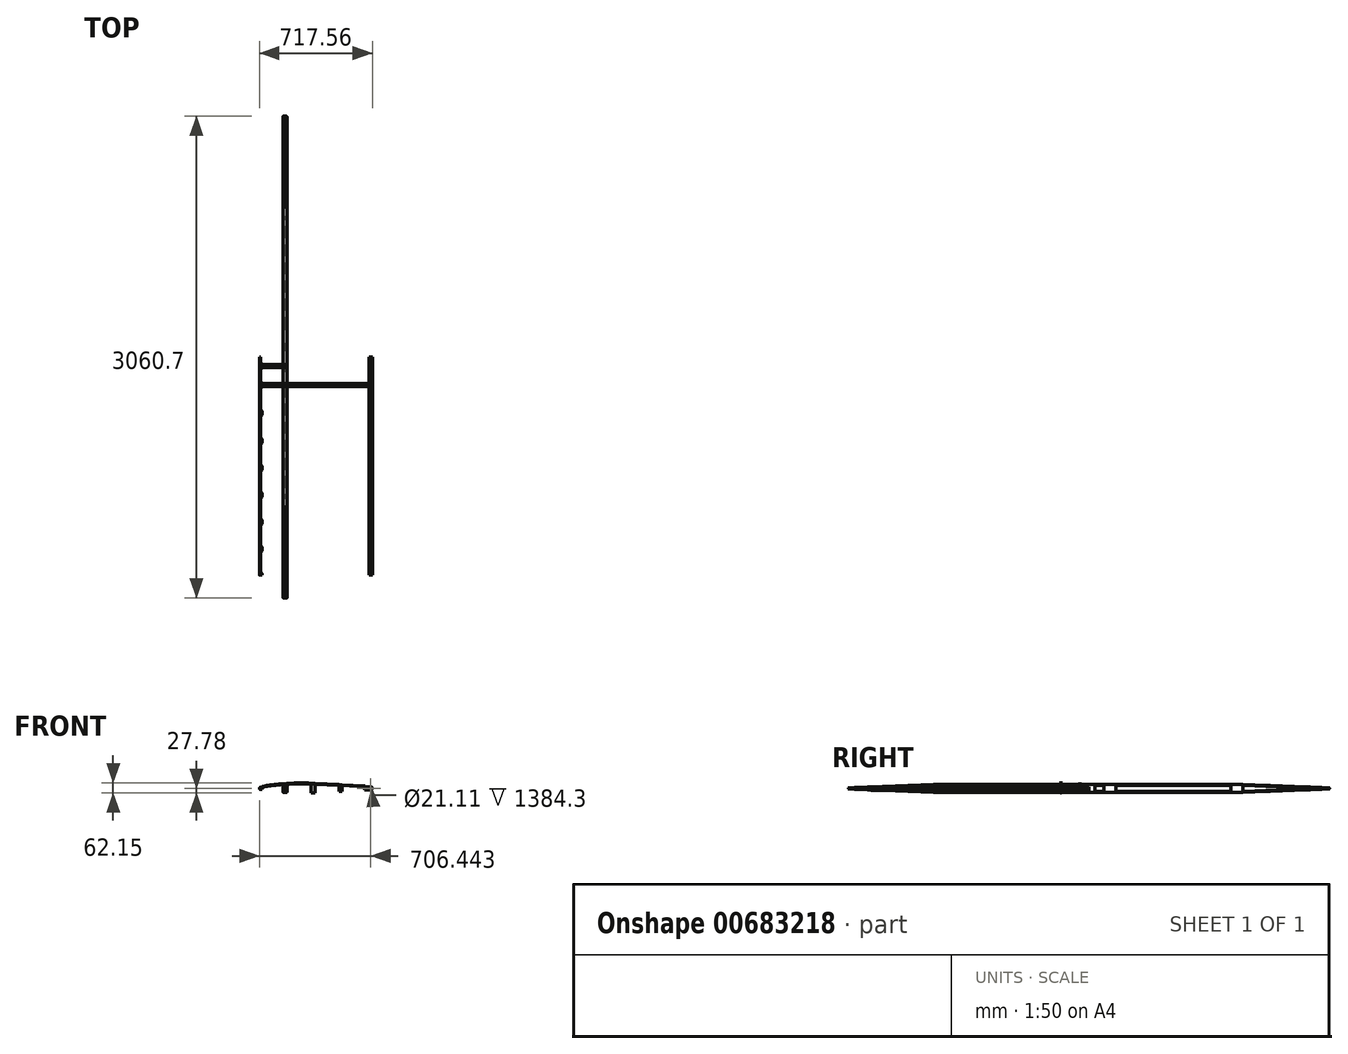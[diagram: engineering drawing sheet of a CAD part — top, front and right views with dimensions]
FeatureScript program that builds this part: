
annotation { "Feature Type Name" : "Feature", "Feature Type Description" : "" }
export const myFeature = defineFeature(function(context is Context, id is Id, definition is map)
    precondition{}
    {
        {
            var Q0;
            Q0=qCreatedBy(makeId("Front.planeOp"),FACE);
            var sketch = newSketch(context, id + "F0", { "sketchPlane" : qUnion([Q0])});
            skLineSegment(sketch, "E0", {"start": v(-12.7, 23.81) * mm, "end": v(12.7, 25.4) * mm});
            skLineSegment(sketch, "E1", {"start": v(12.7, 25.4) * mm, "end": v(12.7, -25.4) * mm});
            skLineSegment(sketch, "E2", {"start": v(12.7, -25.4) * mm, "end": v(-12.7, -23.81) * mm});
            skLineSegment(sketch, "E3", {"start": v(-12.7, -23.81) * mm, "end": v(-12.7, 23.81) * mm});
            skCircle(sketch, "E4", {"center": v(544.51, 0) * mm, "radius": 10.55 * mm});
            skCircle(sketch, "E5", {"center": v(544.51, 0) * mm, "radius": 11.11 * mm});
            skArc(sketch, "E6", {"start": v(-154.56, 7.92) * mm, "mid": v(-161.92, 0) * mm, "end": v(-154.56, -7.92) * mm});
            skLineSegment(sketch, "E7", {"start": v(-154.56, 7.92) * mm, "end": v(-153.99, 5.16) * mm});
            skLineSegment(sketch, "E8", {"start": v(-153.99, -5.16) * mm, "end": v(-154.56, -7.92) * mm});
            skLineSegment(sketch, "E9", {"start": v(-153.99, 5.16) * mm, "end": v(-144.46, 7.14) * mm});
            skLineSegment(sketch, "E10", {"start": v(-144.46, 7.14) * mm, "end": v(-144.46, -7.14) * mm});
            skLineSegment(sketch, "E11", {"start": v(-144.46, -7.14) * mm, "end": v(-153.99, -5.16) * mm});
            skLineSegment(sketch, "E12", {"start": v(-161.93, 0) * mm, "end": v(-161.93, -20.21) * mm, "construction": true});
            skPoint(sketch, "E12.startSnap0", {"position": v(-161.93, 0) * mm});
            skLineSegment(sketch, "E13", {"start": v(-153.99, 5.16) * mm, "end": v(-153.99, -5.16) * mm, "construction": true});
            skLineSegment(sketch, "E14", {"start": v(-161.93, 0) * mm, "end": v(-144.46, 0) * mm, "construction": true});
            skSolve(sketch);
        }
        {
            var Q0;
            Q0=makeQuery(id+"F0.imprint","IMPRINT",FACE,{"disambiguationData":[TD([[makeQuery(id+"F0.imprint","IMPRINT",EDGE,{"derivedFrom":sQuery(id+"F0.wireOp",EDGE,"E0")}),-1.0]])]});
            extrude(context, id + "F1", {"entities" : qUnion([Q0]), "depth" : 952.5 * mm, "offsetDistance" : 25.4 * mm});
        }
        {
            var Q0;
            Q0=makeQuery(id+"F1.opExtrude","SWEPT_FACE",FACE,{"disambiguationData":[OSD([sQuery(id+"F0.wireOp",EDGE,"E3")])]});
            var sketch = newSketch(context, id + "F2", { "sketchPlane" : qUnion([Q0])});
            skLineSegment(sketch, "E15", {"start": v(952.5, 23.81) * mm, "end": v(1530.35, 3.17) * mm});
            skLineSegment(sketch, "E16", {"start": v(952.5, -23.81) * mm, "end": v(1530.35, -3.17) * mm});
            skArc(sketch, "E17", {"start": v(1530.35, 3.18) * mm, "mid": v(1527.18, 0) * mm, "end": v(1530.35, -3.18) * mm});
            skLineSegment(sketch, "E18", {"start": v(1530.35, 0) * mm, "end": v(1530.35, 10.29) * mm, "construction": true});
            skArc(sketch, "E19", {"start": v(1531, 3.1) * mm, "mid": v(1527.18, 0) * mm, "end": v(1531, -3.1) * mm});
            skArc(sketch, "E20", {"start": v(1538.67, 1.5) * mm, "mid": v(1539.88, 0) * mm, "end": v(1538.67, -1.5) * mm});
            skLineSegment(sketch, "E21", {"start": v(1531, 3.1) * mm, "end": v(1538.67, 1.5) * mm});
            skLineSegment(sketch, "E22", {"start": v(1531, -3.1) * mm, "end": v(1538.67, -1.5) * mm});
            skLineSegment(sketch, "E23", {"start": v(1527.18, 0) * mm, "end": v(1527.18, 5.45) * mm, "construction": true});
            skLineSegment(sketch, "E24", {"start": v(1539.88, 0) * mm, "end": v(1539.88, 5.45) * mm, "construction": true});
            skSolve(sketch);
        }
        {
            var Q0;
            Q0=makeQuery(id+"F1.opExtrude","SWEPT_FACE",FACE,{"disambiguationData":[OSD([sQuery(id+"F0.wireOp",EDGE,"E1")])]});
            var sketch = newSketch(context, id + "F3", { "sketchPlane" : qUnion([Q0])});
            skLineSegment(sketch, "E25", {"start": v(-952.5, 25.4) * mm, "end": v(-1530.35, 3.17) * mm});
            skLineSegment(sketch, "E26", {"start": v(-952.5, -25.4) * mm, "end": v(-1530.35, -3.17) * mm});
            skArc(sketch, "E27", {"start": v(-1530.35, 3.18) * mm, "mid": v(-1527.18, 0) * mm, "end": v(-1530.35, -3.18) * mm});
            skSolve(sketch);
        }
        {
            var Q1;
            {var subQ0=sQuery(id+"F2.wireOp",EDGE,"E15");Q1=makeQuery(id+"F2.imprint","IMPRINT",FACE,{"disambiguationData":[TD([[makeQuery(id+"F2.imprint","IMPRINT",EDGE,{"derivedFrom":subQ0}),-1.0]])]});}
            var Q2;
            Q2=makeQuery(id+"F3.imprint","IMPRINT",FACE,{"disambiguationData":[TD([[makeQuery(id+"F3.imprint","IMPRINT",EDGE,{"derivedFrom":sQuery(id+"F3.wireOp",EDGE,"E25")}),1.0]])]});
            loft(context, id + "F4", {"operationType" : NewBodyOperationType.ADD, "sheetProfilesArray" : [{ "sheetProfileEntities" : qUnion([Q1]) }, { "sheetProfileEntities" : qUnion([Q2]) }]});
        }
        {
            var Q0;
            {var subQ0=sQuery(id+"F2.wireOp",EDGE,"E15");var subQ2=sQuery(id+"F0.wireOp",EDGE,"E3");Q0=makeQuery(id+"F4.boolean.opBoolean","MERGE",FACE,{"derivedFrom":[makeQuery(id+"F1.opExtrude","SWEPT_FACE",FACE,{"disambiguationData":[OSD([subQ2])]}),makeQuery(id+"F4.opLoft","CAP_FACE",FACE,{"disambiguationData":[OSD([makeQuery(id+"F2.imprint","IMPRINT",FACE,{"disambiguationData":[TD([[makeQuery(id+"F2.imprint","IMPRINT",EDGE,{"derivedFrom":subQ0}),-1.0]])]})])],"isStart":true})]});}
            var sketch = newSketch(context, id + "F5", { "sketchPlane" : qUnion([Q0])});
            skLineSegment(sketch, "E28.bottom", {"start": v(44.45, 17.46) * mm, "end": v(88.9, 17.46) * mm});
            skLineSegment(sketch, "E28.top", {"start": v(44.45, -17.46) * mm, "end": v(88.9, -17.46) * mm});
            skLineSegment(sketch, "E28.left", {"start": v(38.1, 11.11) * mm, "end": v(38.1, -11.11) * mm});
            skLineSegment(sketch, "E28.right", {"start": v(95.25, 11.11) * mm, "end": v(95.25, -11.11) * mm});
            skPoint(sketch, "E29.visualSharp", {"position": v(38.1, 17.46) * mm});
            skArc(sketch, "E29.filletArc", {"start": v(44.45, 17.46) * mm, "mid": v(39.96, 15.6) * mm, "end": v(38.1, 11.11) * mm});
            skPoint(sketch, "E30.visualSharp", {"position": v(95.25, -17.46) * mm});
            skArc(sketch, "E30.filletArc", {"start": v(88.9, -17.46) * mm, "mid": v(93.4, -15.6) * mm, "end": v(95.25, -11.11) * mm});
            skPoint(sketch, "E31.visualSharp", {"position": v(95.25, 17.46) * mm});
            skArc(sketch, "E31.filletArc", {"start": v(95.25, 11.11) * mm, "mid": v(93.4, 15.6) * mm, "end": v(88.9, 17.46) * mm});
            skPoint(sketch, "E32.visualSharp", {"position": v(38.1, -17.46) * mm});
            skArc(sketch, "E32.filletArc", {"start": v(38.1, -11.11) * mm, "mid": v(39.96, -15.6) * mm, "end": v(44.45, -17.46) * mm});
            skLineSegment(sketch, "E33.bottom", {"start": v(177.8, 17.46) * mm, "end": v(895.35, 17.46) * mm});
            skLineSegment(sketch, "E33.top", {"start": v(177.8, -17.46) * mm, "end": v(895.35, -17.46) * mm});
            skLineSegment(sketch, "E33.left", {"start": v(171.45, 11.11) * mm, "end": v(171.45, -11.11) * mm});
            skLineSegment(sketch, "E33.right", {"start": v(901.7, 11.11) * mm, "end": v(901.7, -11.11) * mm});
            skPoint(sketch, "E34.visualSharp", {"position": v(171.45, 17.46) * mm});
            skArc(sketch, "E34.filletArc", {"start": v(177.8, 17.46) * mm, "mid": v(173.3, 15.6) * mm, "end": v(171.45, 11.11) * mm});
            skPoint(sketch, "E35.visualSharp", {"position": v(171.45, -17.46) * mm});
            skArc(sketch, "E35.filletArc", {"start": v(171.45, -11.11) * mm, "mid": v(173.3, -15.6) * mm, "end": v(177.8, -17.46) * mm});
            skPoint(sketch, "E36.visualSharp", {"position": v(901.7, 17.46) * mm});
            skArc(sketch, "E36.filletArc", {"start": v(901.7, 11.11) * mm, "mid": v(899.84, 15.6) * mm, "end": v(895.35, 17.46) * mm});
            skPoint(sketch, "E37.visualSharp", {"position": v(901.7, -17.46) * mm});
            skArc(sketch, "E37.filletArc", {"start": v(895.35, -17.46) * mm, "mid": v(899.84, -15.6) * mm, "end": v(901.7, -11.11) * mm});
            skLineSegment(sketch, "E38", {"start": v(977.9, 9.97) * mm, "end": v(977.9, -9.97) * mm});
            skLineSegment(sketch, "E39", {"start": v(984.48, -16.32) * mm, "end": v(1329.65, -3.99) * mm});
            skLineSegment(sketch, "E40", {"start": v(1329.65, 3.99) * mm, "end": v(984.48, 16.32) * mm});
            skPoint(sketch, "E41.visualSharp", {"position": v(1441.34, 0) * mm});
            skArc(sketch, "E41.filletArc", {"start": v(1329.65, -3.99) * mm, "mid": v(1333.5, 0) * mm, "end": v(1329.65, 3.99) * mm});
            skPoint(sketch, "E42.visualSharp", {"position": v(977.9, 16.55) * mm});
            skArc(sketch, "E42.filletArc", {"start": v(984.48, 16.32) * mm, "mid": v(979.84, 14.54) * mm, "end": v(977.9, 9.97) * mm});
            skPoint(sketch, "E43.visualSharp", {"position": v(977.9, -16.55) * mm});
            skArc(sketch, "E43.filletArc", {"start": v(977.9, -9.97) * mm, "mid": v(979.84, -14.54) * mm, "end": v(984.48, -16.32) * mm});
            skLineSegment(sketch, "E44", {"start": v(1333.5, 0) * mm, "end": v(1333.5, 29.1) * mm, "construction": true});
            skSolve(sketch);
        }
        {
            var Q0;
            Q0 = qSketchRegion(id + "F5", true);
            extrude(context, id + "F6", {"entities" : qUnion([Q0]), "operationType" : NewBodyOperationType.REMOVE, "oppositeDirection" : true, "depth" : 5 / 406.4 * mm, "offsetDistance" : 25.4 * mm});
        }
        {
            var Q0;
            {var subQ0=sQuery(id+"F0.wireOp",EDGE,"E1");Q0=makeQuery(id+"F4.boolean.opBoolean","MERGE",FACE,{"derivedFrom":[makeQuery(id+"F1.opExtrude","SWEPT_FACE",FACE,{"disambiguationData":[OSD([subQ0])]}),makeQuery(id+"F4.opLoft","CAP_FACE",FACE,{"disambiguationData":[OSD([makeQuery(id+"F3.imprint","IMPRINT",FACE,{"disambiguationData":[TD([[makeQuery(id+"F3.imprint","IMPRINT",EDGE,{"derivedFrom":sQuery(id+"F3.wireOp",EDGE,"E25")}),1.0]])]})])],"isStart":true})]});}
            var sketch = newSketch(context, id + "F7", { "sketchPlane" : qUnion([Q0])});
            skLineSegment(sketch, "E45.bottom", {"start": v(-88.9, 19.05) * mm, "end": v(-44.45, 19.05) * mm});
            skLineSegment(sketch, "E45.top", {"start": v(-88.9, -19.05) * mm, "end": v(-44.45, -19.05) * mm});
            skLineSegment(sketch, "E45.left", {"start": v(-95.25, 12.7) * mm, "end": v(-95.25, -12.7) * mm});
            skLineSegment(sketch, "E45.right", {"start": v(-38.1, 12.7) * mm, "end": v(-38.1, -12.7) * mm});
            skPoint(sketch, "E46.visualSharp", {"position": v(-95.25, 19.05) * mm});
            skArc(sketch, "E46.filletArc", {"start": v(-88.9, 19.05) * mm, "mid": v(-93.4, 17.2) * mm, "end": v(-95.25, 12.7) * mm});
            skPoint(sketch, "E47.visualSharp", {"position": v(-95.25, -19.05) * mm});
            skArc(sketch, "E47.filletArc", {"start": v(-95.25, -12.7) * mm, "mid": v(-93.4, -17.2) * mm, "end": v(-88.9, -19.05) * mm});
            skPoint(sketch, "E48.visualSharp", {"position": v(-38.1, -19.05) * mm});
            skArc(sketch, "E48.filletArc", {"start": v(-44.45, -19.05) * mm, "mid": v(-39.96, -17.2) * mm, "end": v(-38.1, -12.7) * mm});
            skPoint(sketch, "E49.visualSharp", {"position": v(-38.1, 19.05) * mm});
            skArc(sketch, "E49.filletArc", {"start": v(-38.1, 12.7) * mm, "mid": v(-39.96, 17.2) * mm, "end": v(-44.45, 19.05) * mm});
            skLineSegment(sketch, "E50.bottom", {"start": v(-177.8, 19.05) * mm, "end": v(-895.35, 19.05) * mm});
            skLineSegment(sketch, "E50.top", {"start": v(-177.8, -19.05) * mm, "end": v(-895.35, -19.05) * mm});
            skLineSegment(sketch, "E50.left", {"start": v(-171.45, 12.7) * mm, "end": v(-171.45, -12.7) * mm});
            skLineSegment(sketch, "E50.right", {"start": v(-901.7, 12.7) * mm, "end": v(-901.7, -12.7) * mm});
            skPoint(sketch, "E51.visualSharp", {"position": v(-901.7, 19.05) * mm});
            skArc(sketch, "E51.filletArc", {"start": v(-895.35, 19.05) * mm, "mid": v(-899.84, 17.2) * mm, "end": v(-901.7, 12.7) * mm});
            skPoint(sketch, "E52.visualSharp", {"position": v(-901.7, -19.05) * mm});
            skArc(sketch, "E52.filletArc", {"start": v(-901.7, -12.7) * mm, "mid": v(-899.84, -17.2) * mm, "end": v(-895.35, -19.05) * mm});
            skPoint(sketch, "E53.visualSharp", {"position": v(-171.45, 19.05) * mm});
            skArc(sketch, "E53.filletArc", {"start": v(-171.45, 12.7) * mm, "mid": v(-173.3, 17.2) * mm, "end": v(-177.8, 19.05) * mm});
            skPoint(sketch, "E54.visualSharp", {"position": v(-171.45, -19.05) * mm});
            skArc(sketch, "E54.filletArc", {"start": v(-177.8, -19.05) * mm, "mid": v(-173.3, -17.2) * mm, "end": v(-171.45, -12.7) * mm});
            skLineSegment(sketch, "E55", {"start": v(-977.9, 11.47) * mm, "end": v(-977.9, -11.47) * mm});
            skLineSegment(sketch, "E56", {"start": v(-984.5, -17.81) * mm, "end": v(-1329.68, -4.54) * mm});
            skLineSegment(sketch, "E57", {"start": v(-984.5, 17.81) * mm, "end": v(-1329.68, 4.54) * mm});
            skPoint(sketch, "E58.visualSharp", {"position": v(-977.9, 18.07) * mm});
            skArc(sketch, "E58.filletArc", {"start": v(-977.9, 11.47) * mm, "mid": v(-979.85, 16.05) * mm, "end": v(-984.5, 17.81) * mm});
            skPoint(sketch, "E59.visualSharp", {"position": v(-977.9, -18.07) * mm});
            skArc(sketch, "E59.filletArc", {"start": v(-984.5, -17.81) * mm, "mid": v(-979.85, -16.05) * mm, "end": v(-977.9, -11.47) * mm});
            skArc(sketch, "E60.filletArc", {"start": v(-1329.68, 4.54) * mm, "mid": v(-1334.05, 0) * mm, "end": v(-1329.68, -4.54) * mm});
            skSolve(sketch);
        }
        {
            var Q0;
            Q0 = qSketchRegion(id + "F7", true);
            extrude(context, id + "F8", {"entities" : qUnion([Q0]), "operationType" : NewBodyOperationType.REMOVE, "oppositeDirection" : true, "depth" : 7.94 * mm, "offsetDistance" : 25.4 * mm});
        }
        {
            var Q0;
            Q0=makeQuery(id+"F8.boolean.opBoolean","COPY",FACE,{"derivedFrom":makeQuery(id+"F8.opExtrude","CAP_FACE",FACE,{"disambiguationData":[OSD([sQuery(id+"F7.wireOp",EDGE,"E50.bottom"),sQuery(id+"F7.wireOp",EDGE,"E50.top"),sQuery(id+"F7.wireOp",EDGE,"E50.left"),sQuery(id+"F7.wireOp",EDGE,"E50.right"),sQuery(id+"F7.wireOp",EDGE,"E51.filletArc"),sQuery(id+"F7.wireOp",EDGE,"E52.filletArc"),sQuery(id+"F7.wireOp",EDGE,"E53.filletArc"),sQuery(id+"F7.wireOp",EDGE,"E54.filletArc")])],"isStart":false})});
            var Q1;
            Q1=makeQuery(id+"F8.boolean.opBoolean","COPY",FACE,{"derivedFrom":makeQuery(id+"F8.opExtrude","CAP_FACE",FACE,{"disambiguationData":[OSD([sQuery(id+"F7.wireOp",EDGE,"E45.bottom"),sQuery(id+"F7.wireOp",EDGE,"E45.top"),sQuery(id+"F7.wireOp",EDGE,"E45.left"),sQuery(id+"F7.wireOp",EDGE,"E45.right"),sQuery(id+"F7.wireOp",EDGE,"E46.filletArc"),sQuery(id+"F7.wireOp",EDGE,"E47.filletArc"),sQuery(id+"F7.wireOp",EDGE,"E48.filletArc"),sQuery(id+"F7.wireOp",EDGE,"E49.filletArc")])],"isStart":false})});
            var Q2;
            Q2=makeQuery(id+"F6.boolean.opBoolean","COPY",FACE,{"derivedFrom":makeQuery(id+"F6.opExtrude","CAP_FACE",FACE,{"disambiguationData":[OSD([sQuery(id+"F5.wireOp",EDGE,"E33.bottom"),sQuery(id+"F5.wireOp",EDGE,"E33.top"),sQuery(id+"F5.wireOp",EDGE,"E33.left"),sQuery(id+"F5.wireOp",EDGE,"E33.right"),sQuery(id+"F5.wireOp",EDGE,"E34.filletArc"),sQuery(id+"F5.wireOp",EDGE,"E35.filletArc"),sQuery(id+"F5.wireOp",EDGE,"E36.filletArc"),sQuery(id+"F5.wireOp",EDGE,"E37.filletArc")])],"isStart":false})});
            var Q3;
            Q3=makeQuery(id+"F6.boolean.opBoolean","COPY",FACE,{"derivedFrom":makeQuery(id+"F6.opExtrude","CAP_FACE",FACE,{"disambiguationData":[OSD([sQuery(id+"F5.wireOp",EDGE,"E28.bottom"),sQuery(id+"F5.wireOp",EDGE,"E28.top"),sQuery(id+"F5.wireOp",EDGE,"E28.left"),sQuery(id+"F5.wireOp",EDGE,"E28.right"),sQuery(id+"F5.wireOp",EDGE,"E29.filletArc"),sQuery(id+"F5.wireOp",EDGE,"E30.filletArc"),sQuery(id+"F5.wireOp",EDGE,"E31.filletArc"),sQuery(id+"F5.wireOp",EDGE,"E32.filletArc")])],"isStart":false})});
            fillet(context, id + "F9", {"entities" : qUnion([Q0, Q1, Q2, Q3]), "radius" : 9.52 * mm, "tangentPropagation" : true, "allowEdgeOverflow" : false});
        }
        {
            var Q0;
            Q0=makeQuery(id+"F8.boolean.opBoolean","COPY",FACE,{"derivedFrom":makeQuery(id+"F8.opExtrude","CAP_FACE",FACE,{"disambiguationData":[OSD([sQuery(id+"F7.wireOp",EDGE,"E55"),sQuery(id+"F7.wireOp",EDGE,"E56"),sQuery(id+"F7.wireOp",EDGE,"E57"),sQuery(id+"F7.wireOp",EDGE,"E58.filletArc"),sQuery(id+"F7.wireOp",EDGE,"E59.filletArc"),sQuery(id+"F7.wireOp",EDGE,"E60.filletArc")])],"isStart":false})});
            var Q1;
            Q1=makeQuery(id+"F6.boolean.opBoolean","COPY",FACE,{"derivedFrom":makeQuery(id+"F6.opExtrude","CAP_FACE",FACE,{"disambiguationData":[OSD([sQuery(id+"F5.wireOp",EDGE,"E38"),sQuery(id+"F5.wireOp",EDGE,"E39"),sQuery(id+"F5.wireOp",EDGE,"E40"),sQuery(id+"F5.wireOp",EDGE,"E41.filletArc"),sQuery(id+"F5.wireOp",EDGE,"E42.filletArc"),sQuery(id+"F5.wireOp",EDGE,"E43.filletArc")])],"isStart":false})});
            fillet(context, id + "F10", {"entities" : qUnion([Q0, Q1]), "radius" : 6.35 * mm, "tangentPropagation" : true, "allowEdgeOverflow" : false});
        }
        {
            var Q0;
            Q0=makeQuery(id+"F4.opLoft","MID_CAP_EDGE",EDGE,{"disambiguationData":[OSD([sQuery(id+"F0.wireOp",EDGE,"E0"),sQuery(id+"F0.wireOp",EDGE,"E1"),sQuery(id+"F3.wireOp",EDGE,"E25"),sQuery(id+"F3.wireOp",EDGE,"E27")])],"capPos":1.0});
            var Q1;
            Q1=makeQuery(id+"F1.opExtrude","SWEPT_EDGE",EDGE,{"disambiguationData":[OSD([sQuery(id+"F0.wireOp",EDGE,"E0"),sQuery(id+"F0.wireOp",EDGE,"E1")])]});
            var Q2;
            Q2=makeQuery(id+"F1.opExtrude","SWEPT_EDGE",EDGE,{"disambiguationData":[OSD([sQuery(id+"F0.wireOp",EDGE,"E0"),sQuery(id+"F0.wireOp",EDGE,"E3")])]});
            var Q3;
            Q3=makeQuery(id+"F4.opLoft","MID_CAP_EDGE",EDGE,{"disambiguationData":[OSD([sQuery(id+"F0.wireOp",EDGE,"E0"),sQuery(id+"F0.wireOp",EDGE,"E3"),sQuery(id+"F2.wireOp",EDGE,"E15"),sQuery(id+"F2.wireOp",EDGE,"E19")])],"capPos":0.0});
            var Q4;
            Q4=makeQuery(id+"F1.opExtrude","SWEPT_EDGE",EDGE,{"disambiguationData":[OSD([sQuery(id+"F0.wireOp",EDGE,"E2"),sQuery(id+"F0.wireOp",EDGE,"E3")])]});
            var Q5;
            Q5=makeQuery(id+"F4.opLoft","MID_CAP_EDGE",EDGE,{"disambiguationData":[OSD([sQuery(id+"F0.wireOp",EDGE,"E2"),sQuery(id+"F0.wireOp",EDGE,"E3"),sQuery(id+"F2.wireOp",EDGE,"E16"),sQuery(id+"F2.wireOp",EDGE,"E19")])],"capPos":0.0});
            var Q6;
            Q6=makeQuery(id+"F1.opExtrude","SWEPT_EDGE",EDGE,{"disambiguationData":[OSD([sQuery(id+"F0.wireOp",EDGE,"E1"),sQuery(id+"F0.wireOp",EDGE,"E2")])]});
            var Q7;
            Q7=makeQuery(id+"F4.opLoft","MID_CAP_EDGE",EDGE,{"disambiguationData":[OSD([sQuery(id+"F0.wireOp",EDGE,"E1"),sQuery(id+"F0.wireOp",EDGE,"E2"),sQuery(id+"F3.wireOp",EDGE,"E26"),sQuery(id+"F3.wireOp",EDGE,"E27")])],"capPos":1.0});
            fillet(context, id + "F11", {"entities" : qUnion([Q0, Q1, Q2, Q3, Q4, Q5, Q6, Q7]), "radius" : 1.59 * mm, "tangentPropagation" : true, "allowEdgeOverflow" : false});
        }
        {
            var Q0;
            Q0=makeQuery(id+"F1.opExtrude","SWEPT_BODY",BODY,{"disambiguationData":[OSD([sQuery(id+"F0.wireOp",EDGE,"E0"),sQuery(id+"F0.wireOp",EDGE,"E1"),sQuery(id+"F0.wireOp",EDGE,"E2"),sQuery(id+"F0.wireOp",EDGE,"E3")])]});
            var Q1;
            Q1=qCreatedBy(makeId("Front.planeOp"),FACE);
            mirror(context, id + "F12", {"operationType" : NewBodyOperationType.ADD, "entities" : qUnion([Q0]), "mirrorPlane" : qUnion([Q1])});
        }
        {
            var Q0;
            Q0=makeQuery(id+"F0.imprint","IMPRINT",FACE,{"disambiguationData":[TD([[makeQuery(id+"F0.imprint","IMPRINT",EDGE,{"derivedFrom":sQuery(id+"F0.wireOp",EDGE,"E6")}),1.0]])]});
            extrude(context, id + "F13", {"entities" : qUnion([Q0]), "depth" : 1384.3 * mm, "offsetDistance" : 25.4 * mm});
        }
        {
            var Q0;
            Q0=qCreatedBy(makeId("Top.planeOp"),FACE);
            var sketch = newSketch(context, id + "F14", { "sketchPlane" : qUnion([Q0])});
            skLineSegment(sketch, "E61.bottom", {"start": v(-144.46, -44.45) * mm, "end": v(-138.9, -44.45) * mm});
            skLineSegment(sketch, "E61.top", {"start": v(-154.78, 6.35) * mm, "end": v(-138.9, 6.35) * mm});
            skLineSegment(sketch, "E61.left", {"start": v(-154.78, -27.52) * mm, "end": v(-154.78, 6.35) * mm});
            skLineSegment(sketch, "E61.right", {"start": v(-138.9, -44.45) * mm, "end": v(-138.9, 6.35) * mm});
            skPoint(sketch, "E62.visualSharp", {"position": v(-154.78, -44.45) * mm});
            skArc(sketch, "E62.filletArc", {"start": v(-154.78, -27.52) * mm, "mid": v(-152, -37.43) * mm, "end": v(-144.46, -44.45) * mm});
            skPoint(sketch, "E63.visualSharp", {"position": v(-154.78, 6.35) * mm});
            skLineSegment(sketch, "E64.bottom", {"start": v(-144.46, -165.1) * mm, "end": v(-138.9, -165.1) * mm});
            skLineSegment(sketch, "E64.top", {"start": v(-144.46, -69.85) * mm, "end": v(-138.9, -69.85) * mm});
            skLineSegment(sketch, "E64.left", {"start": v(-154.78, -148.17) * mm, "end": v(-154.78, -86.78) * mm});
            skLineSegment(sketch, "E64.right", {"start": v(-138.9, -165.1) * mm, "end": v(-138.9, -69.85) * mm});
            skPoint(sketch, "E65.visualSharp", {"position": v(-154.78, -69.85) * mm});
            skArc(sketch, "E65.filletArc", {"start": v(-144.46, -69.85) * mm, "mid": v(-152, -76.87) * mm, "end": v(-154.78, -86.78) * mm});
            skPoint(sketch, "E66.visualSharp", {"position": v(-154.78, -165.1) * mm});
            skArc(sketch, "E66.filletArc", {"start": v(-154.78, -148.17) * mm, "mid": v(-152, -158.08) * mm, "end": v(-144.46, -165.1) * mm});
            skLineSegment(sketch, "E67.bottom", {"start": v(-144.46, -342.9) * mm, "end": v(-138.9, -342.9) * mm});
            skLineSegment(sketch, "E67.top", {"start": v(-144.46, -190.5) * mm, "end": v(-138.9, -190.5) * mm});
            skLineSegment(sketch, "E67.left", {"start": v(-154.78, -325.97) * mm, "end": v(-154.78, -207.43) * mm});
            skLineSegment(sketch, "E67.right", {"start": v(-138.9, -342.9) * mm, "end": v(-138.9, -190.5) * mm});
            skPoint(sketch, "E68.visualSharp", {"position": v(-154.78, -342.9) * mm});
            skArc(sketch, "E68.filletArc", {"start": v(-154.78, -325.97) * mm, "mid": v(-152, -335.88) * mm, "end": v(-144.46, -342.9) * mm});
            skPoint(sketch, "E69.visualSharp", {"position": v(-154.78, -190.5) * mm});
            skArc(sketch, "E69.filletArc", {"start": v(-144.46, -190.5) * mm, "mid": v(-152, -197.52) * mm, "end": v(-154.78, -207.43) * mm});
            skLineSegment(sketch, "E70.bottom", {"start": v(-144.46, -520.7) * mm, "end": v(-138.9, -520.7) * mm});
            skLineSegment(sketch, "E70.top", {"start": v(-144.46, -368.3) * mm, "end": v(-138.9, -368.3) * mm});
            skLineSegment(sketch, "E70.left", {"start": v(-154.78, -503.77) * mm, "end": v(-154.78, -385.23) * mm});
            skLineSegment(sketch, "E70.right", {"start": v(-138.9, -520.7) * mm, "end": v(-138.9, -368.3) * mm});
            skPoint(sketch, "E71.visualSharp", {"position": v(-154.78, -520.7) * mm});
            skArc(sketch, "E71.filletArc", {"start": v(-154.78, -503.77) * mm, "mid": v(-152, -513.68) * mm, "end": v(-144.46, -520.7) * mm});
            skPoint(sketch, "E72.visualSharp", {"position": v(-154.78, -368.3) * mm});
            skArc(sketch, "E72.filletArc", {"start": v(-144.46, -368.3) * mm, "mid": v(-152, -375.32) * mm, "end": v(-154.78, -385.23) * mm});
            skLineSegment(sketch, "E73.bottom", {"start": v(-144.46, -692.15) * mm, "end": v(-138.9, -692.15) * mm});
            skLineSegment(sketch, "E73.top", {"start": v(-144.46, -546.1) * mm, "end": v(-138.9, -546.1) * mm});
            skLineSegment(sketch, "E73.left", {"start": v(-154.78, -675.22) * mm, "end": v(-154.78, -563.03) * mm});
            skLineSegment(sketch, "E73.right", {"start": v(-138.9, -692.15) * mm, "end": v(-138.9, -546.1) * mm});
            skPoint(sketch, "E74.visualSharp", {"position": v(-154.78, -692.15) * mm});
            skArc(sketch, "E74.filletArc", {"start": v(-154.78, -675.22) * mm, "mid": v(-152, -685.13) * mm, "end": v(-144.46, -692.15) * mm});
            skPoint(sketch, "E75.visualSharp", {"position": v(-154.78, -546.1) * mm});
            skArc(sketch, "E75.filletArc", {"start": v(-144.46, -546.1) * mm, "mid": v(-152, -553.12) * mm, "end": v(-154.78, -563.03) * mm});
            skLineSegment(sketch, "E76.bottom", {"start": v(-144.46, -863.6) * mm, "end": v(-138.9, -863.6) * mm});
            skLineSegment(sketch, "E76.top", {"start": v(-144.46, -717.55) * mm, "end": v(-138.9, -717.55) * mm});
            skLineSegment(sketch, "E76.left", {"start": v(-154.78, -846.67) * mm, "end": v(-154.78, -734.48) * mm});
            skLineSegment(sketch, "E76.right", {"start": v(-138.9, -863.6) * mm, "end": v(-138.9, -717.55) * mm});
            skPoint(sketch, "E77.visualSharp", {"position": v(-154.78, -863.6) * mm});
            skArc(sketch, "E77.filletArc", {"start": v(-154.78, -846.67) * mm, "mid": v(-152, -856.58) * mm, "end": v(-144.46, -863.6) * mm});
            skPoint(sketch, "E78.visualSharp", {"position": v(-154.78, -717.55) * mm});
            skArc(sketch, "E78.filletArc", {"start": v(-144.46, -717.55) * mm, "mid": v(-152, -724.57) * mm, "end": v(-154.78, -734.48) * mm});
            skLineSegment(sketch, "E79.bottom", {"start": v(-144.46, -1035.05) * mm, "end": v(-138.9, -1035.05) * mm});
            skLineSegment(sketch, "E79.top", {"start": v(-144.46, -889) * mm, "end": v(-138.9, -889) * mm});
            skLineSegment(sketch, "E79.left", {"start": v(-154.78, -1018.12) * mm, "end": v(-154.78, -905.93) * mm});
            skLineSegment(sketch, "E79.right", {"start": v(-138.9, -1035.05) * mm, "end": v(-138.9, -889) * mm});
            skPoint(sketch, "E80.visualSharp", {"position": v(-154.78, -1035.05) * mm});
            skArc(sketch, "E80.filletArc", {"start": v(-154.78, -1018.12) * mm, "mid": v(-152, -1028.03) * mm, "end": v(-144.46, -1035.05) * mm});
            skPoint(sketch, "E81.visualSharp", {"position": v(-154.78, -889) * mm});
            skArc(sketch, "E81.filletArc", {"start": v(-144.46, -889) * mm, "mid": v(-152, -896.02) * mm, "end": v(-154.78, -905.93) * mm});
            skLineSegment(sketch, "E82.bottom", {"start": v(-144.46, -1206.5) * mm, "end": v(-138.9, -1206.5) * mm});
            skLineSegment(sketch, "E82.top", {"start": v(-144.46, -1060.45) * mm, "end": v(-138.9, -1060.45) * mm});
            skLineSegment(sketch, "E82.left", {"start": v(-154.78, -1189.57) * mm, "end": v(-154.78, -1077.38) * mm});
            skLineSegment(sketch, "E82.right", {"start": v(-138.9, -1206.5) * mm, "end": v(-138.9, -1060.45) * mm});
            skPoint(sketch, "E83.visualSharp", {"position": v(-154.78, -1206.5) * mm});
            skArc(sketch, "E83.filletArc", {"start": v(-154.78, -1189.57) * mm, "mid": v(-152, -1199.48) * mm, "end": v(-144.46, -1206.5) * mm});
            skPoint(sketch, "E84.visualSharp", {"position": v(-154.78, -1060.45) * mm});
            skArc(sketch, "E84.filletArc", {"start": v(-144.46, -1060.45) * mm, "mid": v(-152, -1067.47) * mm, "end": v(-154.78, -1077.38) * mm});
            skLineSegment(sketch, "E85.bottom", {"start": v(-144.46, -1374.78) * mm, "end": v(-138.9, -1374.78) * mm});
            skLineSegment(sketch, "E85.top", {"start": v(-144.46, -1231.9) * mm, "end": v(-138.9, -1231.9) * mm});
            skLineSegment(sketch, "E85.left", {"start": v(-154.78, -1357.84) * mm, "end": v(-154.78, -1248.83) * mm});
            skLineSegment(sketch, "E85.right", {"start": v(-138.9, -1374.78) * mm, "end": v(-138.9, -1231.9) * mm});
            skPoint(sketch, "E86.visualSharp", {"position": v(-154.78, -1374.78) * mm});
            skArc(sketch, "E86.filletArc", {"start": v(-154.78, -1357.84) * mm, "mid": v(-152, -1367.76) * mm, "end": v(-144.46, -1374.78) * mm});
            skPoint(sketch, "E87.visualSharp", {"position": v(-154.78, -1231.9) * mm});
            skArc(sketch, "E87.filletArc", {"start": v(-144.46, -1231.9) * mm, "mid": v(-152, -1238.92) * mm, "end": v(-154.78, -1248.83) * mm});
            skLineSegment(sketch, "E88", {"start": v(-144.46, -1389.7) * mm, "end": v(-144.46, 6.35) * mm, "construction": true});
            skSolve(sketch);
        }
        {
            var Q0;
            Q0 = qSketchRegion(id + "F14", true);
            extrude(context, id + "F15", {"entities" : qUnion([Q0]), "operationType" : NewBodyOperationType.REMOVE, "endBound" : BoundingType.SYMMETRIC, "oppositeDirection" : true, "depth" : 25.4 * mm, "offsetDistance" : 25.4 * mm});
        }
        {
            var Q0;
            Q0=qCreatedBy(makeId("Front.planeOp"),FACE);
            cPlane(context, id + "F16", {"entities" : qUnion([Q0]), "cplaneType" : CPlaneType.OFFSET, "offset" : 57.15 * mm, "width" : 152.4 * mm, "height" : 152.4 * mm});
        }
        {
            var Q0;
            Q0=qCreatedBy(makeId("Front.planeOp"),FACE);
            cPlane(context, id + "F17", {"entities" : qUnion([Q0]), "cplaneType" : CPlaneType.OFFSET, "offset" : 177.8 * mm, "width" : 152.4 * mm, "height" : 152.4 * mm});
        }
        {
            var Q0;
            Q0=makeQuery(id+"F0.imprint","IMPRINT",FACE,{"disambiguationData":[TD([[makeQuery(id+"F0.imprint","IMPRINT",EDGE,{"derivedFrom":sQuery(id+"F0.wireOp",EDGE,"E4")}),-1.0]])]});
            extrude(context, id + "F18", {"entities" : qUnion([Q0]), "depth" : 1384.3 * mm, "offsetDistance" : 25.4 * mm});
        }
        {
            var Q0;
            Q0=qCreatedBy(id+"F17.planeOp",FACE);
            var sketch = newSketch(context, id + "F19", { "sketchPlane" : qUnion([Q0])});
            skLineSegment(sketch, "E89.bottom", {"start": v(165.1, 27.78) * mm, "end": v(190.5, 26.99) * mm});
            skLineSegment(sketch, "E89.top", {"start": v(165.1, -27.78) * mm, "end": v(190.5, -26.99) * mm});
            skLineSegment(sketch, "E89.left", {"start": v(165.1, 27.78) * mm, "end": v(165.1, -27.78) * mm});
            skLineSegment(sketch, "E89.right", {"start": v(190.5, 26.99) * mm, "end": v(190.5, -26.99) * mm});
            skLineSegment(sketch, "E90", {"start": v(177.8, 27.38) * mm, "end": v(177.8, -27.38) * mm, "construction": true});
            skPoint(sketch, "E90.endSnap0", {"position": v(177.8, -27.38) * mm});
            skLineSegment(sketch, "E91.bottom", {"start": v(342.9, 19.84) * mm, "end": v(361.95, 19.05) * mm});
            skLineSegment(sketch, "E91.top", {"start": v(342.9, -19.84) * mm, "end": v(361.95, -19.05) * mm});
            skLineSegment(sketch, "E91.left", {"start": v(342.9, 19.84) * mm, "end": v(342.9, -19.84) * mm});
            skLineSegment(sketch, "E91.right", {"start": v(361.95, 19.05) * mm, "end": v(361.95, -19.05) * mm});
            skLineSegment(sketch, "E92", {"start": v(352.43, 19.45) * mm, "end": v(352.43, -19.45) * mm, "construction": true});
            skPoint(sketch, "E92.endSnap0", {"position": v(352.43, -19.45) * mm});
            skLineSegment(sketch, "E93", {"start": v(537.64, 8.73) * mm, "end": v(504.83, 10.72) * mm});
            skLineSegment(sketch, "E94", {"start": v(504.83, 10.72) * mm, "end": v(504.83, -10.72) * mm});
            skLineSegment(sketch, "E95", {"start": v(504.83, -10.72) * mm, "end": v(537.64, -8.73) * mm});
            skArc(sketch, "E96", {"start": v(537.64, 8.73) * mm, "mid": v(533.4, 0) * mm, "end": v(537.64, -8.73) * mm});
            skLineSegment(sketch, "E97", {"start": v(533.4, 0) * mm, "end": v(533.4, -19.02) * mm});
            skLineSegment(sketch, "E98", {"start": v(-153.99, 5.16) * mm, "end": v(-154.56, 7.92) * mm});
            skLineSegment(sketch, "E99", {"start": v(12.7, 25.4) * mm, "end": v(12.7, 30.16) * mm, "construction": true});
            skLineSegment(sketch, "E100", {"start": v(-154.56, 7.92) * mm, "end": v(-144.46, 12.03) * mm});
            skArc(sketch, "E101", {"start": v(12.7, 25.4) * mm, "mid": v(-71.1, 19.11) * mm, "end": v(-153.99, 5.16) * mm});
            skLineSegment(sketch, "E102", {"start": v(12.7, 25.4) * mm, "end": v(12.7, 23.71) * mm, "construction": true});
            skLineSegment(sketch, "E103", {"start": v(12.7, 25.4) * mm, "end": v(11.01, 25.3) * mm, "construction": true});
            skArc(sketch, "E104", {"start": v(12.7, 30.16) * mm, "mid": v(-66.27, 24.48) * mm, "end": v(-144.46, 12.03) * mm});
            skArc(sketch, "E105", {"start": v(537.64, 8.73) * mm, "mid": v(540.96, 10.53) * mm, "end": v(544.7, 11.11) * mm});
            skLineSegment(sketch, "E106", {"start": v(510.28, 15.16) * mm, "end": v(510.18, 13.94) * mm});
            skLineSegment(sketch, "E107", {"start": v(510.18, 13.94) * mm, "end": v(544.7, 11.11) * mm});
            skLineSegment(sketch, "E108", {"start": v(342.9, 19.84) * mm, "end": v(190.5, 26.99) * mm});
            skLineSegment(sketch, "E109", {"start": v(504.83, 15.49) * mm, "end": v(510.28, 15.16) * mm});
            skLineSegment(sketch, "E110", {"start": v(361.95, 19.05) * mm, "end": v(504.83, 10.72) * mm});
            skLineSegment(sketch, "E111", {"start": v(511.66, 15.06) * mm, "end": v(545.43, 12.62) * mm});
            skArc(sketch, "E112", {"start": v(545.43, 12.62) * mm, "mid": v(557.16, -0.18) * mm, "end": v(545.06, -12.64) * mm});
            skLineSegment(sketch, "E113", {"start": v(545.06, -12.64) * mm, "end": v(513.73, -14) * mm});
            skLineSegment(sketch, "E114", {"start": v(362.12, 23.81) * mm, "end": v(342.9, 24.61) * mm});
            skLineSegment(sketch, "E115", {"start": v(342.9, 24.61) * mm, "end": v(190.5, 31.76) * mm});
            skLineSegment(sketch, "E116", {"start": v(190.5, 31.76) * mm, "end": v(165.1, 32.53) * mm});
            skArc(sketch, "E117", {"start": v(12.7, 25.4) * mm, "mid": v(88.85, 29.5) * mm, "end": v(165.1, 27.78) * mm});
            skArc(sketch, "E118", {"start": v(12.7, 30.16) * mm, "mid": v(88.85, 34.25) * mm, "end": v(165.1, 32.53) * mm});
            skLineSegment(sketch, "E119", {"start": v(362.12, 23.81) * mm, "end": v(504.83, 15.49) * mm});
            skSolve(sketch);
        }
        {
            var Q0;
            Q0=makeQuery(id+"F19.imprint","IMPRINT",FACE,{"disambiguationData":[TD([[makeQuery(id+"F19.imprint","IMPRINT",EDGE,{"derivedFrom":sQuery(id+"F19.wireOp",EDGE,"E89.bottom")}),-1.0]])]});
            extrude(context, id + "F20", {"entities" : qUnion([Q0]), "endBound" : BoundingType.SYMMETRIC, "depth" : 6.35 * mm, "offsetDistance" : 25.4 * mm});
        }
        {
            var Q0;
            Q0=makeQuery(id+"F19.imprint","IMPRINT",FACE,{"disambiguationData":[TD([[makeQuery(id+"F19.imprint","IMPRINT",EDGE,{"derivedFrom":sQuery(id+"F19.wireOp",EDGE,"E91.bottom")}),-1.0]])]});
            extrude(context, id + "F21", {"entities" : qUnion([Q0]), "endBound" : BoundingType.SYMMETRIC, "depth" : 6.35 * mm, "offsetDistance" : 25.4 * mm});
        }
        {
            var Q0;
            {var subQ1=sQuery(id+"F19.wireOp",EDGE,"E93");Q0=makeQuery(id+"F19.imprint","IMPRINT",FACE,{"disambiguationData":[TD([[makeQuery(id+"F19.imprint","IMPRINT",EDGE,{"derivedFrom":subQ1}),1.0]])]});}
            extrude(context, id + "F22", {"entities" : qUnion([Q0]), "endBound" : BoundingType.SYMMETRIC, "depth" : 19.05 * mm, "offsetDistance" : 25.4 * mm});
        }
        {
            var Q0;
            Q0=qCreatedBy(id+"F16.planeOp",FACE);
            var sketch = newSketch(context, id + "F23", { "sketchPlane" : qUnion([Q0])});
            skLineSegment(sketch, "E120", {"start": v(-153.99, 5.16) * mm, "end": v(-154.56, 7.92) * mm});
            skLineSegment(sketch, "E121", {"start": v(12.7, 25.4) * mm, "end": v(12.7, 28.58) * mm});
            skLineSegment(sketch, "E122", {"start": v(-154.56, 7.92) * mm, "end": v(-144.46, 10.4) * mm});
            skArc(sketch, "E123", {"start": v(12.7, 25.4) * mm, "mid": v(-71.1, 19.11) * mm, "end": v(-153.99, 5.16) * mm});
            skLineSegment(sketch, "E124", {"start": v(12.7, 25.4) * mm, "end": v(12.7, 23.71) * mm, "construction": true});
            skLineSegment(sketch, "E125", {"start": v(12.7, 25.4) * mm, "end": v(11.01, 25.3) * mm, "construction": true});
            skArc(sketch, "E126", {"start": v(12.7, 28.58) * mm, "mid": v(-66.27, 22.88) * mm, "end": v(-144.46, 10.4) * mm});
            skSolve(sketch);
        }
        {
            var Q0;
            Q0=makeQuery(id+"F23.imprint","IMPRINT",FACE,{"disambiguationData":[TD([[makeQuery(id+"F23.imprint","IMPRINT",EDGE,{"derivedFrom":sQuery(id+"F23.wireOp",EDGE,"E120")}),-1.0]])]});
            extrude(context, id + "F24", {"entities" : qUnion([Q0]), "endBound" : BoundingType.SYMMETRIC, "depth" : 19.05 * mm, "offsetDistance" : 25.4 * mm});
        }
        {
            var Q0;
            Q0=makeQuery(id+"F24.opExtrude","SWEPT_EDGE",EDGE,{"disambiguationData":[OSD([sQuery(id+"F23.wireOp",EDGE,"E121"),sQuery(id+"F23.wireOp",EDGE,"E126")])]});
            fillet(context, id + "F25", {"entities" : qUnion([Q0]), "radius" : 1.59 * mm, "tangentPropagation" : true, "allowEdgeOverflow" : false});
        }
        {
            var Q0;
            Q0=makeQuery(id+"F24.opExtrude","CAP_EDGE",EDGE,{"disambiguationData":[OSD([sQuery(id+"F23.wireOp",EDGE,"E126")])],"isStart":false});
            var Q1;
            Q1=makeQuery(id+"F24.opExtrude","CAP_EDGE",EDGE,{"disambiguationData":[OSD([sQuery(id+"F23.wireOp",EDGE,"E126")])],"isStart":true});
            var Q2;
            Q2=makeQuery(id+"F24.opExtrude","CAP_EDGE",EDGE,{"disambiguationData":[OSD([sQuery(id+"F23.wireOp",EDGE,"E122")])],"isStart":false});
            var Q3;
            Q3=makeQuery(id+"F24.opExtrude","CAP_EDGE",EDGE,{"disambiguationData":[OSD([sQuery(id+"F23.wireOp",EDGE,"E122")])],"isStart":true});
            fillet(context, id + "F26", {"entities" : qUnion([Q0, Q1, Q2, Q3]), "radius" : 1.59 * mm, "tangentPropagation" : true, "allowEdgeOverflow" : false});
        }
        {
            var Q0;
            Q0=makeQuery(id+"F19.imprint","IMPRINT",FACE,{"disambiguationData":[TD([[makeQuery(id+"F19.imprint","IMPRINT",EDGE,{"derivedFrom":sQuery(id+"F19.wireOp",EDGE,"E89.bottom")}),1.0]])]});
            extrude(context, id + "F27", {"entities" : qUnion([Q0]), "endBound" : BoundingType.SYMMETRIC, "depth" : 19.05 * mm, "offsetDistance" : 25.4 * mm});
        }
    });
